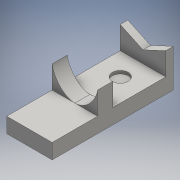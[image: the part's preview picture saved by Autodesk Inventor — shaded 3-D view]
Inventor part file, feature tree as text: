
AUTODESK INVENTOR PART (.ipt)
format: ipt  version: 2016 (Build 200138000, 138)  size: 147,968 bytes
history: native  units: mm
features: extrude x5, sketch x5, projected_geometry x1
ambient origin geometry x8: Origin, YZ Plane, XZ Plane, XY Plane, X Axis, Y Axis, Z Axis, Center Point
bodies: Solid1 (feature_tree)
feature tree (11):
  extrude  "Extrusion1"  Depth=10.0mm
  extrude  "Extrusion2"  Depth=10.0mm TaperAngle=0.0deg
  extrude  "Extrusion3"  Depth=5.0mm TaperAngle=0.0deg
  extrude  "Extrusion4"  TaperAngle=0.0deg  [1 undecoded]
  extrude  "Extrusion5"  Depth=5.0mm
  sketch  "Sketch1"  dims[d0=10.0mm d1=0.0mm d2=30.0mm]
  sketch  "Sketch2"  dims[d3=30.0mm d4=10.0mm d5=0.0mm]
  sketch  "Sketch3"  dims[d6=50.0mm d7=0.0mm d8=5.0mm d9=0.0mm]
  projected_geometry  "Projected Loop1"
  sketch  "Sketch4"  dims[d16=15.0mm d18=0.0mm]
  sketch  "Sketch5"  dims[d19=5.0mm d20=5.0mm d21=10.5mm d22=20.0mm d23=2.0mm d24=0.0mm d27=8.0mm d28=15.0mm]
note: 1 required parameter value undecoded (feature->parameter linkage not recoverable at this tier; creation-order binding heuristic only, values carry confidence <= 0.55)
